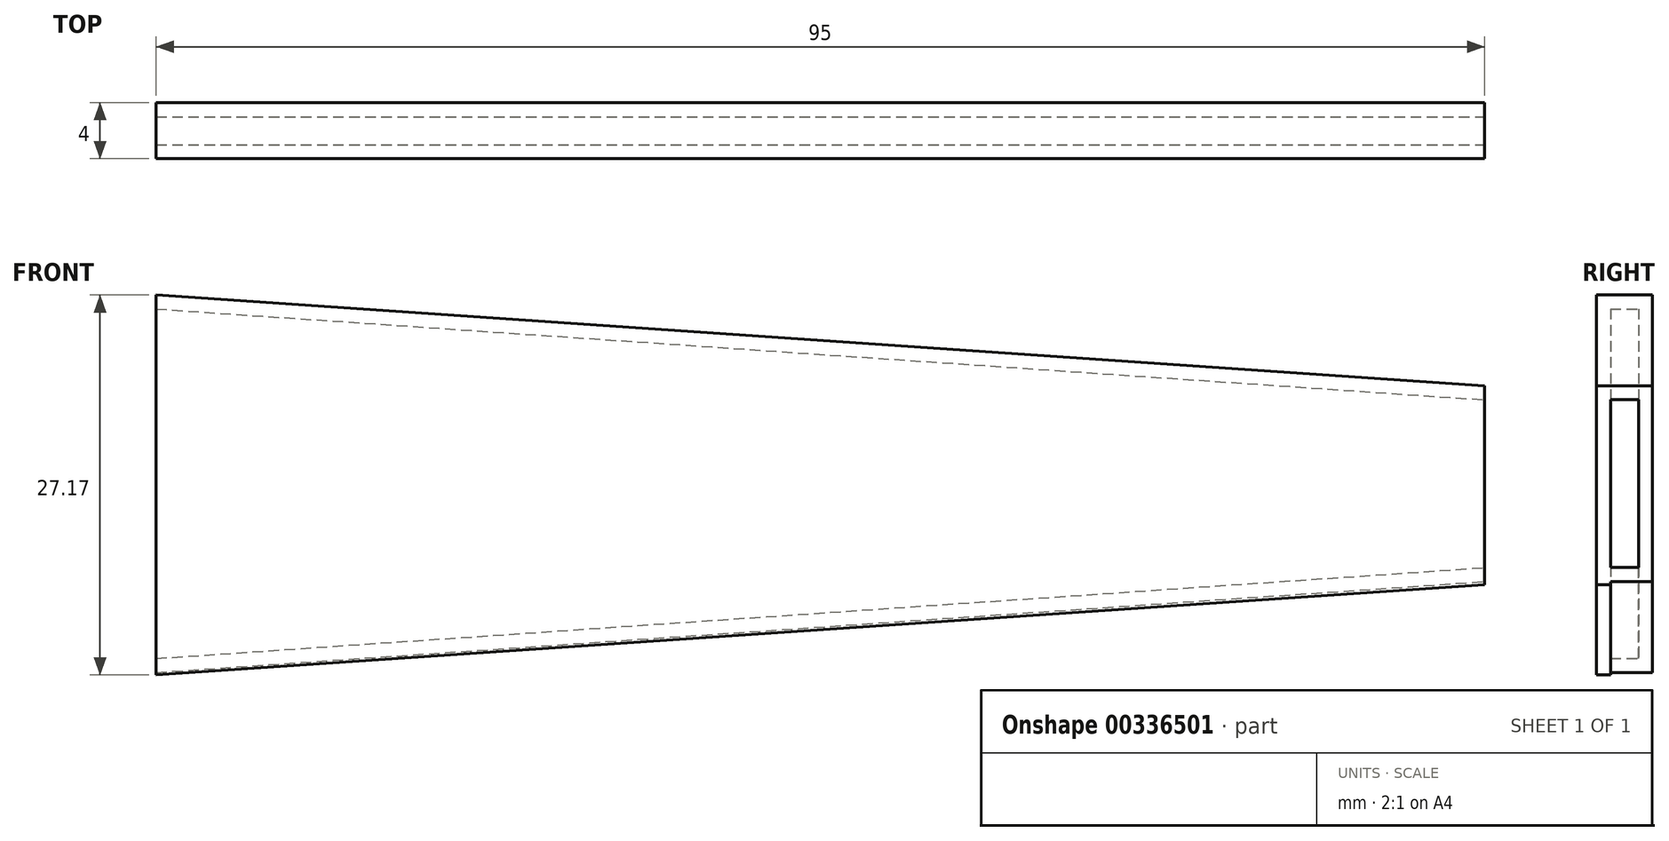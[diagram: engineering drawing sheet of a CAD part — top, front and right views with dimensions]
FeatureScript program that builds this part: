
annotation { "Feature Type Name" : "Feature", "Feature Type Description" : "" }
export const myFeature = defineFeature(function(context is Context, id is Id, definition is map)
    precondition{}
    {
        {
            var Q0;
            Q0=qCreatedBy(makeId("Front.planeOp"),FACE);
            var sketch = newSketch(context, id + "F0", { "sketchPlane" : qUnion([Q0])});
            skLineSegment(sketch, "E0", {"start": v(-47.63, 15.42) * mm, "end": v(-47.63, -11.58) * mm});
            skLineSegment(sketch, "E1", {"start": v(-47.63, -11.58) * mm, "end": v(47.37, -5.08) * mm});
            skLineSegment(sketch, "E2", {"start": v(47.37, -5.08) * mm, "end": v(47.37, 8.92) * mm});
            skLineSegment(sketch, "E3", {"start": v(47.37, 8.92) * mm, "end": v(-47.63, 15.42) * mm});
            skSolve(sketch);
        }
        {
            var Q0;
            Q0=makeQuery(id+"F0.imprint","IMPRINT",FACE,{"disambiguationData":[TD([[makeQuery(id+"F0.imprint","IMPRINT",EDGE,{"derivedFrom":sQuery(id+"F0.wireOp",EDGE,"E0")}),1.0]])]});
            extrude(context, id + "F1", {"entities" : qUnion([Q0]), "depth" : 1 * mm});
        }
        {
            var Q0;
            Q0=makeQuery(id+"F1.opExtrude","CAP_FACE",FACE,{"disambiguationData":[OSD([sQuery(id+"F0.wireOp",EDGE,"E0"),sQuery(id+"F0.wireOp",EDGE,"E1"),sQuery(id+"F0.wireOp",EDGE,"E2"),sQuery(id+"F0.wireOp",EDGE,"E3")])],"isStart":false});
            var sketch = newSketch(context, id + "F2", { "sketchPlane" : qUnion([Q0])});
            skLineSegment(sketch, "E4", {"start": v(-47.63, 15.42) * mm, "end": v(-47.63, 14.42) * mm});
            skLineSegment(sketch, "E5", {"start": v(-47.63, 14.42) * mm, "end": v(47.37, 7.92) * mm});
            skLineSegment(sketch, "E6", {"start": v(47.37, 7.92) * mm, "end": v(47.37, 8.92) * mm});
            skLineSegment(sketch, "E7", {"start": v(47.37, 8.92) * mm, "end": v(-47.63, 15.42) * mm});
            skLineSegment(sketch, "E8", {"start": v(-47.63, -11.58) * mm, "end": v(-47.63, -10.58) * mm});
            skLineSegment(sketch, "E9", {"start": v(-47.63, -10.58) * mm, "end": v(47.37, -4.08) * mm});
            skLineSegment(sketch, "E10", {"start": v(47.37, -4.08) * mm, "end": v(47.37, -5.08) * mm});
            skLineSegment(sketch, "E11", {"start": v(47.37, -5.08) * mm, "end": v(-47.63, -11.58) * mm});
            skSolve(sketch);
        }
        {
            var Q0;
            Q0 = qSketchRegion(id + "F2", true);
            extrude(context, id + "F3", {"entities" : qUnion([Q0]), "operationType" : NewBodyOperationType.ADD, "depth" : 2 * mm});
        }
        {
            var Q0;
            Q0=makeQuery(id+"F3.opExtrude","CAP_FACE",FACE,{"disambiguationData":[OSD([sQuery(id+"F2.wireOp",EDGE,"E4"),sQuery(id+"F2.wireOp",EDGE,"E5"),sQuery(id+"F2.wireOp",EDGE,"E6"),sQuery(id+"F2.wireOp",EDGE,"E7")])],"isStart":false});
            var sketch = newSketch(context, id + "F4", { "sketchPlane" : qUnion([Q0])});
            skLineSegment(sketch, "E12", {"start": v(-47.63, 15.42) * mm, "end": v(-47.63, -11.75) * mm});
            skLineSegment(sketch, "E13", {"start": v(-47.63, -11.75) * mm, "end": v(47.37, -5.31) * mm});
            skLineSegment(sketch, "E14", {"start": v(47.37, -5.31) * mm, "end": v(47.37, 8.92) * mm});
            skLineSegment(sketch, "E15", {"start": v(47.37, 8.92) * mm, "end": v(-47.63, 15.42) * mm});
            skSolve(sketch);
        }
        {
            var Q0;
            Q0 = qSketchRegion(id + "F4", true);
            extrude(context, id + "F5", {"entities" : qUnion([Q0]), "operationType" : NewBodyOperationType.ADD, "depth" : 1 * mm});
        }
    });
